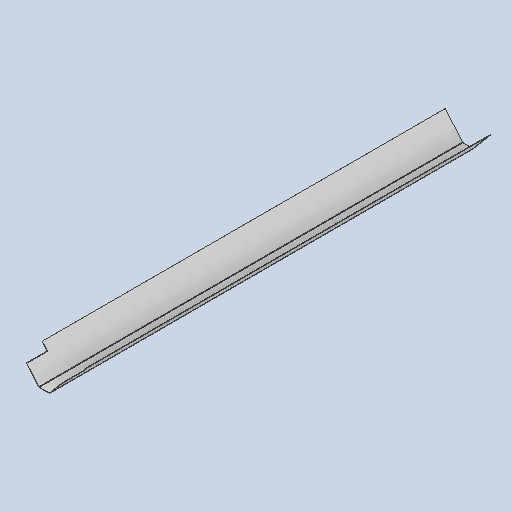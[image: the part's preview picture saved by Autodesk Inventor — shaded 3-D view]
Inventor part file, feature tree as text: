
AUTODESK INVENTOR PART (.ipt)
format: ipt  version: 2025 (Build 290162010, 162A)  size: 326,656 bytes
history: native  units: mm
features: sheet_metal_op x3, sketch x2, other x2, extrude x1
ambient origin geometry x8: Origin, YZ Plane, XZ Plane, XY Plane, X Axis, Y Axis, Z Axis, Center Point
bodies: Body1 (feature_tree)
feature tree (8):
  sheet_metal_op  "Contour Flange2"
  extrude  "Extrusion1"  Depth=50.0mm
  sketch  "Sketch4"  dims[d14=217.819926mm d15=50.0mm]
  other  "Plate5"
  sheet_metal_op  "Bend4"
  sheet_metal_op  "Corner4"
  sketch  "Sketch6"  dims[d16=100.0mm d17=2.0mm d39=22.68928mm d40=2.0mm d41=2.0mm d42=1.0mm d43=4.0mm d44=2.0mm d45=2050.0mm d46=2.0mm d47=2.0mm d48=8.0mm d49=2.0mm d50=2.0mm d51=30.0mm d52=100.0mm d53=0.0mm d54=0.0mm]
  other  "Definition1"
